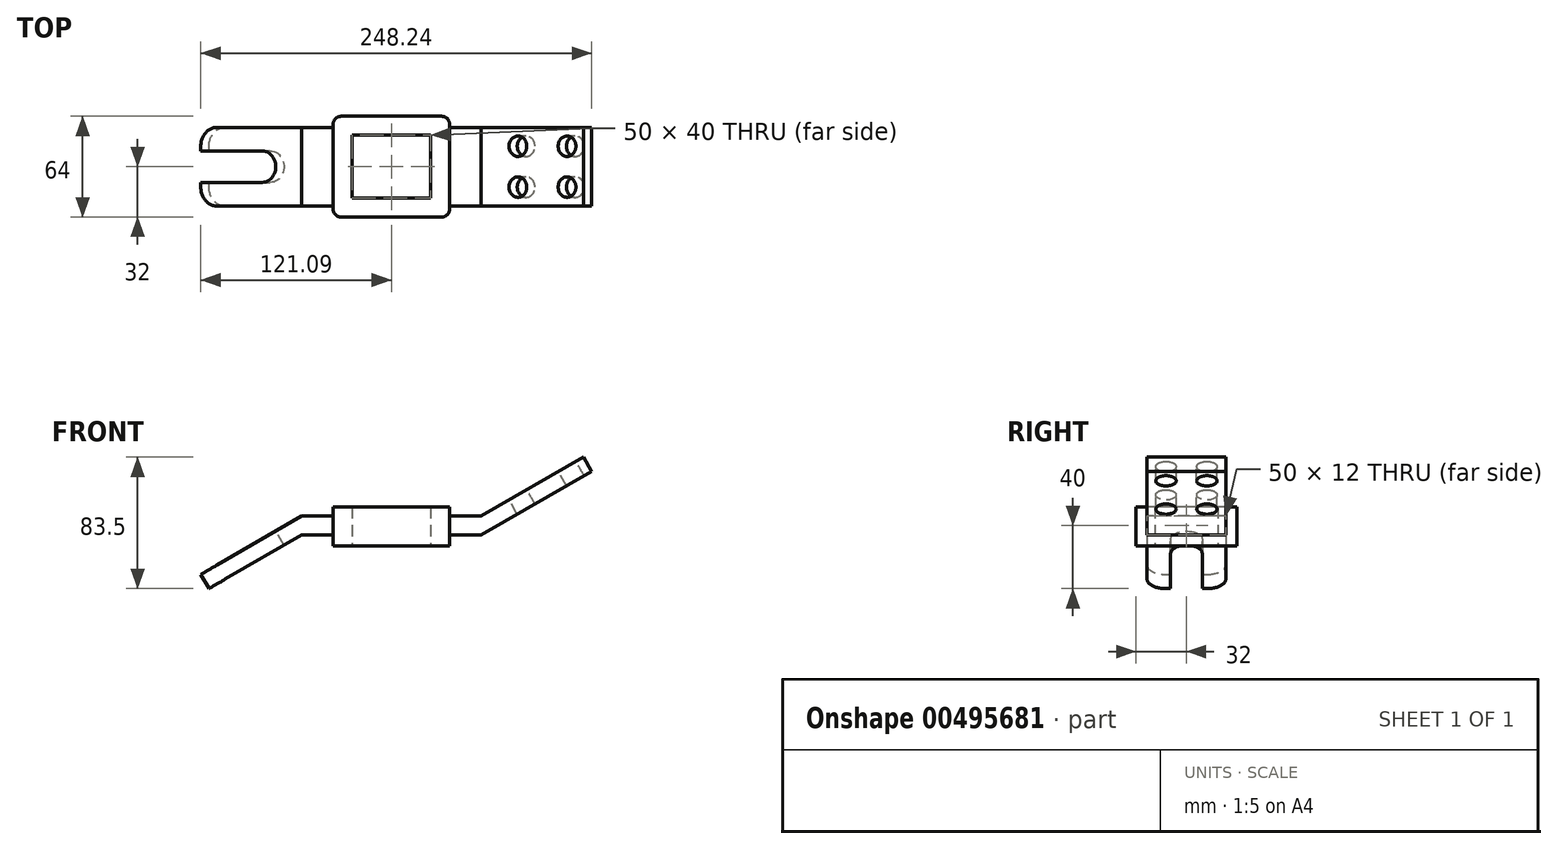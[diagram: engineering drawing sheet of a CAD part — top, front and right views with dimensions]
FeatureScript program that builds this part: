
annotation { "Feature Type Name" : "Feature", "Feature Type Description" : "" }
export const myFeature = defineFeature(function(context is Context, id is Id, definition is map)
    precondition{}
    {
        {
            var Q0;
            Q0=qCreatedBy(makeId("Top.planeOp"),FACE);
            var sketch = newSketch(context, id + "F0", { "sketchPlane" : qUnion([Q0])});
            skLineSegment(sketch, "E0.bottom", {"start": v(37, 32) * mm, "end": v(-37, 32) * mm});
            skLineSegment(sketch, "E0.top", {"start": v(37, -32) * mm, "end": v(-37, -32) * mm});
            skLineSegment(sketch, "E0.left", {"start": v(37, 32) * mm, "end": v(37, -32) * mm});
            skLineSegment(sketch, "E0.right", {"start": v(-37, 32) * mm, "end": v(-37, -32) * mm});
            skPoint(sketch, "E0.middle", {"position": v(0, 0) * mm});
            skLineSegment(sketch, "E1.bottom", {"start": v(25, 20) * mm, "end": v(-25, 20) * mm});
            skLineSegment(sketch, "E1.top", {"start": v(25, -20) * mm, "end": v(-25, -20) * mm});
            skLineSegment(sketch, "E1.left", {"start": v(25, 20) * mm, "end": v(25, -20) * mm});
            skLineSegment(sketch, "E1.right", {"start": v(-25, 20) * mm, "end": v(-25, -20) * mm});
            skSolve(sketch);
        }
        {
            var Q0;
            Q0 = qSketchRegion(id + "F0", true);
            extrude(context, id + "F1", {"entities" : qUnion([Q0]), "depth" : 25 * mm});
        }
        {
            var Q0;
            Q0=makeQuery(id+"F1.opExtrude","SWEPT_FACE",FACE,{"disambiguationData":[OSD([sQuery(id+"F0.wireOp",EDGE,"E0.right")])]});
            var sketch = newSketch(context, id + "F2", { "sketchPlane" : qUnion([Q0])});
            skLineSegment(sketch, "E2.bottom", {"start": v(25, 19) * mm, "end": v(-25, 19) * mm});
            skLineSegment(sketch, "E2.top", {"start": v(25, 7) * mm, "end": v(-25, 7) * mm});
            skLineSegment(sketch, "E2.left", {"start": v(25, 19) * mm, "end": v(25, 7) * mm});
            skLineSegment(sketch, "E2.right", {"start": v(-25, 19) * mm, "end": v(-25, 7) * mm});
            skPoint(sketch, "E2.middle", {"position": v(0, 13) * mm});
            skSolve(sketch);
        }
        {
            var Q0;
            Q0 = qSketchRegion(id + "F2", true);
            extrude(context, id + "F3", {"entities" : qUnion([Q0]), "operationType" : NewBodyOperationType.ADD, "depth" : 20 * mm});
        }
        {
            var Q0;
            Q0=qCreatedBy(makeId("Front.planeOp"),FACE);
            var sketch = newSketch(context, id + "F4", { "sketchPlane" : qUnion([Q0])});
            skLineSegment(sketch, "E3.0.0", {"start": v(-37, 7) * mm, "end": v(-37, 19) * mm});
            skLineSegment(sketch, "E3.0.1", {"start": v(-37, 19) * mm, "end": v(-57, 19) * mm});
            skLineSegment(sketch, "E3.0.2", {"start": v(-57, 19) * mm, "end": v(-57, 7) * mm});
            skLineSegment(sketch, "E3.0.3", {"start": v(-57, 7) * mm, "end": v(-37, 7) * mm});
            skLineSegment(sketch, "E4", {"start": v(-57, 19) * mm, "end": v(-121.09, -18) * mm});
            skLineSegment(sketch, "E5", {"start": v(-57, 19) * mm, "end": v(-114.14, 19) * mm, "construction": true});
            skLineSegment(sketch, "E6", {"start": v(-121.09, -18) * mm, "end": v(-115.89, -27) * mm});
            skLineSegment(sketch, "E7", {"start": v(-57, 7) * mm, "end": v(-115.89, -27) * mm});
            skSolve(sketch);
        }
        {
            var Q0;
            Q0=makeQuery(id+"F4.imprint","IMPRINT",FACE,{"disambiguationData":[TD([[makeQuery(id+"F4.imprint","IMPRINT",EDGE,{"derivedFrom":sQuery(id+"F4.wireOp",EDGE,"E3.0.2")}),-1.0]])]});
            extrude(context, id + "F5", {"entities" : qUnion([Q0]), "operationType" : NewBodyOperationType.ADD, "depth" : 25 * mm, "hasSecondDirection" : true, "secondDirectionOppositeDirection" : true, "secondDirectionDepth" : 25 * mm});
        }
        {
            var Q0;
            Q0=makeQuery(id+"F5.opExtrude","SWEPT_FACE",FACE,{"disambiguationData":[OSD([sQuery(id+"F4.wireOp",EDGE,"E4")])]});
            var sketch = newSketch(context, id + "F6", { "sketchPlane" : qUnion([Q0])});
            skLineSegment(sketch, "E8", {"start": v(-113.86, 25) * mm, "end": v(-68.86, 25) * mm});
            skLineSegment(sketch, "E9", {"start": v(-39.86, 0) * mm, "end": v(-113.86, 0) * mm});
            skCircle(sketch, "E10", {"center": v(-68.86, 0) * mm, "radius": 10 * mm});
            skLineSegment(sketch, "E11", {"start": v(-68.86, 10) * mm, "end": v(-113.86, 10) * mm});
            skLineSegment(sketch, "E12", {"start": v(-68.86, -10) * mm, "end": v(-113.86, -10) * mm});
            skLineSegment(sketch, "E13", {"start": v(-113.86, 25) * mm, "end": v(-113.86, -25) * mm});
            skSolve(sketch);
        }
        {
            var Q0;
            Q0 = qSketchRegion(id + "F6", true);
            extrude(context, id + "F7", {"entities" : qUnion([Q0]), "operationType" : NewBodyOperationType.REMOVE, "oppositeDirection" : true, "depth" : 25 * mm});
        }
        {
            var Q0;
            Q0=makeQuery(id+"F1.opExtrude","SWEPT_FACE",FACE,{"disambiguationData":[OSD([sQuery(id+"F0.wireOp",EDGE,"E0.left")])]});
            var sketch = newSketch(context, id + "F8", { "sketchPlane" : qUnion([Q0])});
            skLineSegment(sketch, "E14.bottom", {"start": v(25, 19) * mm, "end": v(-25, 19) * mm});
            skLineSegment(sketch, "E14.top", {"start": v(25, 7) * mm, "end": v(-25, 7) * mm});
            skLineSegment(sketch, "E14.left", {"start": v(25, 19) * mm, "end": v(25, 7) * mm});
            skLineSegment(sketch, "E14.right", {"start": v(-25, 19) * mm, "end": v(-25, 7) * mm});
            skPoint(sketch, "E14.middle", {"position": v(0, 13) * mm});
            skSolve(sketch);
        }
        {
            var Q0;
            Q0 = qSketchRegion(id + "F8", true);
            extrude(context, id + "F9", {"entities" : qUnion([Q0]), "operationType" : NewBodyOperationType.ADD, "depth" : 20 * mm});
        }
        {
            var Q0;
            Q0=qCreatedBy(makeId("Front.planeOp"),FACE);
            var sketch = newSketch(context, id + "F10", { "sketchPlane" : qUnion([Q0])});
            skLineSegment(sketch, "E15.0.0", {"start": v(37, 19) * mm, "end": v(37, 7) * mm});
            skLineSegment(sketch, "E15.0.1", {"start": v(37, 7) * mm, "end": v(57, 7) * mm});
            skLineSegment(sketch, "E15.0.2", {"start": v(57, 7) * mm, "end": v(57, 19) * mm});
            skLineSegment(sketch, "E15.0.3", {"start": v(57, 19) * mm, "end": v(37, 19) * mm});
            skLineSegment(sketch, "E16", {"start": v(57, 19) * mm, "end": v(121.95, 56.5) * mm});
            skLineSegment(sketch, "E17", {"start": v(57, 7) * mm, "end": v(113.74, 7) * mm, "construction": true});
            skLineSegment(sketch, "E18", {"start": v(121.95, 56.5) * mm, "end": v(131.51, 39.94) * mm});
            skLineSegment(sketch, "E19", {"start": v(57, 7) * mm, "end": v(127.15, 47.5) * mm});
            skSolve(sketch);
        }
        {
            var Q0;
            Q0 = qSketchRegion(id + "F10", true);
            extrude(context, id + "F11", {"entities" : qUnion([Q0]), "operationType" : NewBodyOperationType.ADD, "depth" : 25 * mm, "hasSecondDirection" : true, "secondDirectionOppositeDirection" : true, "secondDirectionDepth" : 25 * mm});
        }
        {
            var Q0;
            Q0=makeQuery(id+"F11.opExtrude","SWEPT_FACE",FACE,{"disambiguationData":[OSD([sQuery(id+"F10.wireOp",EDGE,"E16")])]});
            var sketch = newSketch(context, id + "F12", { "sketchPlane" : qUnion([Q0])});
            skLineSegment(sketch, "E20", {"start": v(133.86, 0) * mm, "end": v(58.86, 0) * mm});
            skLineSegment(sketch, "E21", {"start": v(133.86, 25) * mm, "end": v(121.86, 25) * mm});
            skLineSegment(sketch, "E22", {"start": v(133.86, 25) * mm, "end": v(133.86, 13) * mm});
            skLineSegment(sketch, "E23", {"start": v(133.86, 13) * mm, "end": v(121.86, 13) * mm});
            skCircle(sketch, "E24", {"center": v(121.86, 13) * mm, "radius": 6.5 * mm});
            skCircle(sketch, "E25.MirrorC", {"center": v(121.86, -13) * mm, "radius": 6.5 * mm});
            skLineSegment(sketch, "E26", {"start": v(121.86, 25) * mm, "end": v(96.36, 25) * mm});
            skLineSegment(sketch, "E27", {"start": v(121.86, 25) * mm, "end": v(85.86, 25) * mm});
            skLineSegment(sketch, "E28", {"start": v(85.86, 25) * mm, "end": v(85.86, 13) * mm});
            skCircle(sketch, "E29", {"center": v(85.86, 13) * mm, "radius": 6.5 * mm});
            skCircle(sketch, "E30.MirrorC", {"center": v(85.86, -13) * mm, "radius": 6.5 * mm});
            skSolve(sketch);
        }
        {
            var Q0;
            Q0 = qSketchRegion(id + "F12", true);
            extrude(context, id + "F13", {"entities" : qUnion([Q0]), "operationType" : NewBodyOperationType.REMOVE, "oppositeDirection" : true, "depth" : 25 * mm});
        }
        {
            var Q0;
            Q0=makeQuery(id+"F1.opExtrude","SWEPT_EDGE",EDGE,{"disambiguationData":[OSD([sQuery(id+"F0.wireOp",EDGE,"E0.bottom"),sQuery(id+"F0.wireOp",EDGE,"E0.right")])]});
            var Q1;
            Q1=makeQuery(id+"F1.opExtrude","SWEPT_EDGE",EDGE,{"disambiguationData":[OSD([sQuery(id+"F0.wireOp",EDGE,"E0.bottom"),sQuery(id+"F0.wireOp",EDGE,"E0.left")])]});
            var Q2;
            Q2=makeQuery(id+"F1.opExtrude","SWEPT_EDGE",EDGE,{"disambiguationData":[OSD([sQuery(id+"F0.wireOp",EDGE,"E0.top"),sQuery(id+"F0.wireOp",EDGE,"E0.right")])]});
            var Q3;
            Q3=makeQuery(id+"F1.opExtrude","SWEPT_EDGE",EDGE,{"disambiguationData":[OSD([sQuery(id+"F0.wireOp",EDGE,"E0.top"),sQuery(id+"F0.wireOp",EDGE,"E0.left")])]});
            fillet(context, id + "F14", {"entities" : qUnion([Q0, Q1, Q2, Q3]), "radius" : 5 * mm, "tangentPropagation" : true, "allowEdgeOverflow" : false});
        }
        {
            var Q0;
            Q0=makeQuery(id+"F5.opExtrude","CAP_EDGE",EDGE,{"disambiguationData":[OSD([sQuery(id+"F4.wireOp",EDGE,"E6")])],"isStart":true});
            var Q1;
            Q1=makeQuery(id+"F5.opExtrude","CAP_EDGE",EDGE,{"disambiguationData":[OSD([sQuery(id+"F4.wireOp",EDGE,"E6")])],"isStart":false});
            fillet(context, id + "F15", {"entities" : qUnion([Q0, Q1]), "radius" : 12 * mm, "tangentPropagation" : true, "allowEdgeOverflow" : false});
        }
    });
